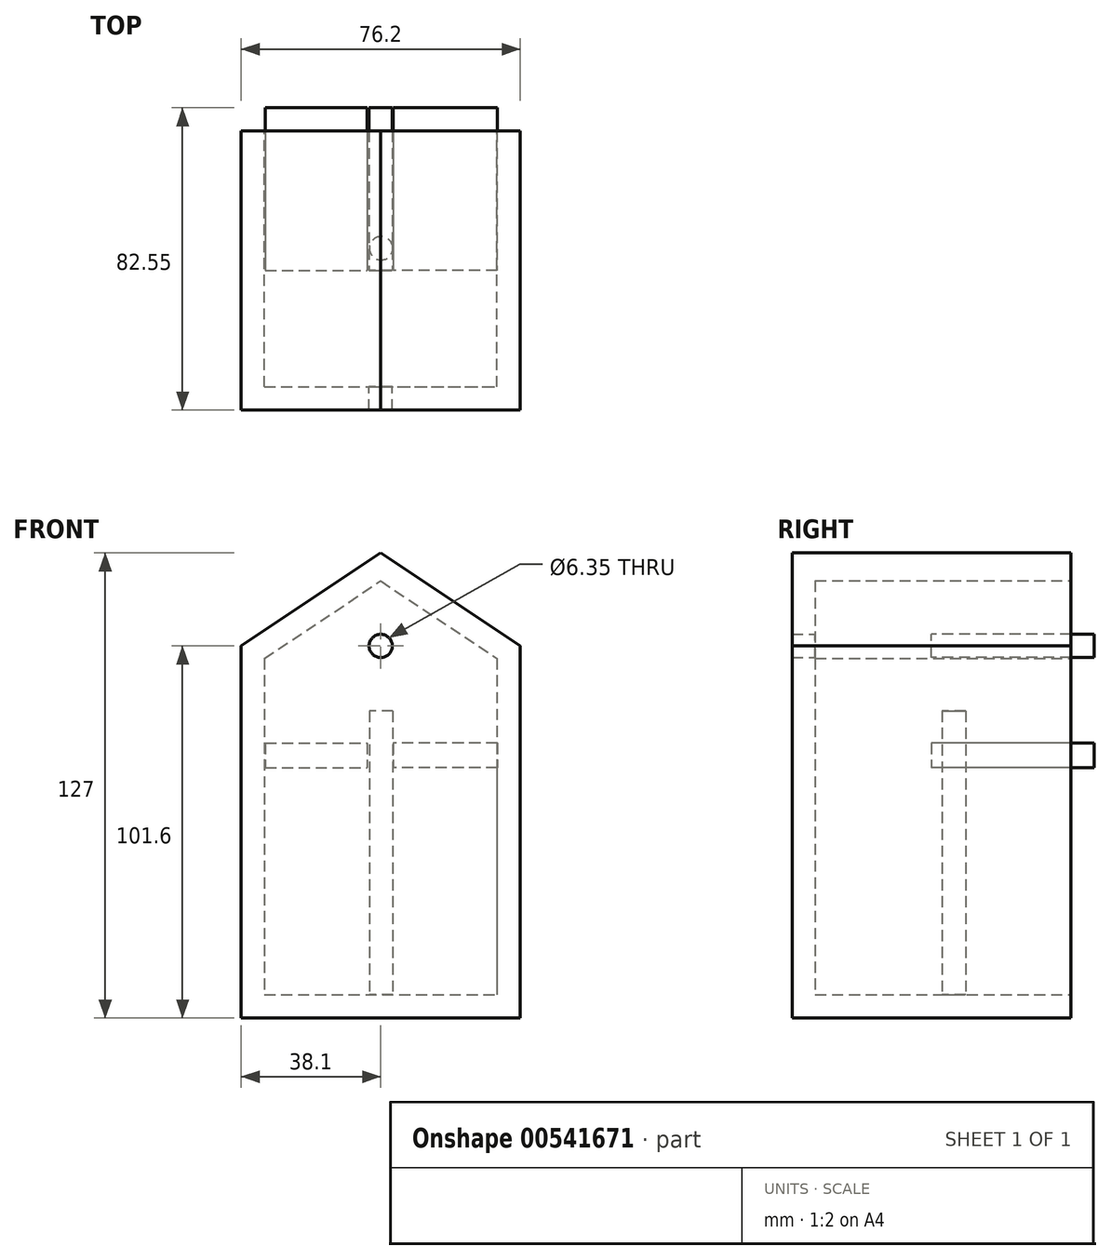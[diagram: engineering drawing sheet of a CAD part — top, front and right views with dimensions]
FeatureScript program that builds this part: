
annotation { "Feature Type Name" : "Feature", "Feature Type Description" : "" }
export const myFeature = defineFeature(function(context is Context, id is Id, definition is map)
    precondition{}
    {
        {
            var Q0;
            Q0=qCreatedBy(makeId("Front.planeOp"),FACE);
            var sketch = newSketch(context, id + "F0", { "sketchPlane" : qUnion([Q0])});
            skLineSegment(sketch, "E0.bottom", {"start": v(-38.1, 50.8) * mm, "end": v(38.1, 50.8) * mm, "construction": true});
            skLineSegment(sketch, "E0.top", {"start": v(-38.1, -50.8) * mm, "end": v(38.1, -50.8) * mm});
            skLineSegment(sketch, "E0.left", {"start": v(-38.1, 50.8) * mm, "end": v(-38.1, -50.8) * mm});
            skLineSegment(sketch, "E0.right", {"start": v(38.1, 50.8) * mm, "end": v(38.1, -50.8) * mm});
            skLineSegment(sketch, "E1", {"start": v(0, 50.8) * mm, "end": v(0, -50.8) * mm, "construction": true});
            skLineSegment(sketch, "E2", {"start": v(-38.1, 50.8) * mm, "end": v(0, 76.2) * mm});
            skLineSegment(sketch, "E3", {"start": v(0, 76.2) * mm, "end": v(38.1, 50.8) * mm});
            skSolve(sketch);
        }
        {
            var Q0;
            Q0=qSketchRegion(id+"F0",true);
            extrude(context, id + "F1", {"entities" : qUnion([Q0]), "endBound" : BoundingType.SYMMETRIC, "depth" : 76.2 * mm});
        }
        {
            var Q0;
            Q0=makeQuery(id+"F1.opExtrude","CAP_FACE",FACE,{"disambiguationData":[OSD([sQuery(id+"F0.wireOp",EDGE,"E0.top"),sQuery(id+"F0.wireOp",EDGE,"E0.left"),sQuery(id+"F0.wireOp",EDGE,"E0.right"),sQuery(id+"F0.wireOp",EDGE,"E2"),sQuery(id+"F0.wireOp",EDGE,"E3")])],"isStart":true});
            shell(context, id + "F2", {"entities" : qUnion([Q0]), "thickness" : 6.35 * mm});
        }
        {
            var Q0;
            Q0=makeQuery(id+"F0.imprint","IMPRINT",FACE,{"disambiguationData":[TD([[makeQuery(id+"F0.imprint","IMPRINT",EDGE,{"derivedFrom":sQuery(id+"F0.wireOp",EDGE,"E0.top")}),1.0]])]});
            var sketch = newSketch(context, id + "F3", { "sketchPlane" : qUnion([Q0])});
            skLineSegment(sketch, "E4.bottom", {"start": v(31.85, 24.31) * mm, "end": v(3.36, 24.31) * mm});
            skLineSegment(sketch, "E4.top", {"start": v(31.85, 17.54) * mm, "end": v(3.36, 17.54) * mm});
            skLineSegment(sketch, "E4.left", {"start": v(31.85, 24.31) * mm, "end": v(31.85, 17.54) * mm});
            skLineSegment(sketch, "E4.right", {"start": v(3.36, 24.31) * mm, "end": v(3.36, 17.54) * mm});
            skLineSegment(sketch, "E5.bottom", {"start": v(-31.54, 24.31) * mm, "end": v(-3.74, 24.31) * mm});
            skLineSegment(sketch, "E5.top", {"start": v(-31.54, 17.54) * mm, "end": v(-3.74, 17.54) * mm});
            skLineSegment(sketch, "E5.left", {"start": v(-31.54, 24.31) * mm, "end": v(-31.54, 17.54) * mm});
            skLineSegment(sketch, "E5.right", {"start": v(-3.74, 24.31) * mm, "end": v(-3.74, 17.54) * mm});
            skSolve(sketch);
        }
        {
            var Q0;
            Q0=sQuery(id+"F3.wireOp",EDGE,"E4.bottom");
            var Q1;
            Q1=sQuery(id+"F3.wireOp",EDGE,"E4.right");
            var Q2;
            Q2=sQuery(id+"F3.wireOp",EDGE,"E4.top");
            var Q3;
            Q3=sQuery(id+"F3.wireOp",EDGE,"E4.left");
            var Q4;
            Q4=sQuery(id+"F3.wireOp",EDGE,"E5.right");
            var Q5;
            Q5=sQuery(id+"F3.wireOp",EDGE,"E5.bottom");
            var Q6;
            Q6=sQuery(id+"F3.wireOp",EDGE,"E5.top");
            var Q7;
            Q7=sQuery(id+"F3.wireOp",EDGE,"E5.left");
            extrude(context, id + "F4", {"bodyType" : ToolBodyType.SURFACE, "surfaceEntities" : qUnion([Q0, Q1, Q2, Q3, Q4, Q5, Q6, Q7]), "endBound" : BoundingType.SYMMETRIC, "oppositeDirection" : true, "depth" : 76.2 * mm});
        }
        {
            var Q0;
            Q0=makeQuery(id+"F2.opShell","OFFSET_FACE",FACE,{"disambiguationData":[OSD([sQuery(id+"F0.wireOp",EDGE,"E0.top")])]});
            var sketch = newSketch(context, id + "F5", { "sketchPlane" : qUnion([Q0])});
            skCircle(sketch, "E6", {"center": v(0.09, 6.08) * mm, "radius": 3.2 * mm});
            skSolve(sketch);
        }
        {
            var Q0;
            Q0=qSketchRegion(id+"F5",true);
            extrude(context, id + "F6", {"entities" : qUnion([Q0]), "operationType" : NewBodyOperationType.ADD, "depth" : 77.51 * mm});
        }
        {
            var Q0;
            Q0=makeQuery(id+"F3.imprint","IMPRINT",FACE,{"disambiguationData":[TD([[makeQuery(id+"F3.imprint","IMPRINT",EDGE,{"derivedFrom":sQuery(id+"F3.wireOp",EDGE,"E4.bottom")}),-1.0]])]});
            var sketch = newSketch(context, id + "F7", { "sketchPlane" : qUnion([Q0])});
            skCircle(sketch, "E7", {"center": v(0, 50.8) * mm, "radius": 3.18 * mm});
            skSolve(sketch);
        }
        {
            var Q0;
            Q0=qSketchRegion(id+"F7",true);
            extrude(context, id + "F8", {"entities" : qUnion([Q0]), "operationType" : NewBodyOperationType.REMOVE, "endBound" : BoundingType.THROUGH_ALL, "depth" : 50.8 * mm});
        }
        {
            var Q0;
            Q0=qSketchRegion(id+"F7",true);
            extrude(context, id + "F10", {"entities" : qUnion([Q0]), "oppositeDirection" : true, "depth" : 44.45 * mm});
        }
        {
            var Q0;
            Q0=qSketchRegion(id+"F3",true);
            extrude(context, id + "F12", {"entities" : qUnion([Q0]), "operationType" : NewBodyOperationType.ADD, "oppositeDirection" : true, "depth" : 44.45 * mm});
        }
        {
            var Q0;
            Q0=qConstructionFilter(qBodyType(qCreatedBy(id+"F5",EDGE),BodyType.WIRE),ConstructionObject.NO);
            extrude(context, id + "F13", {"bodyType" : ToolBodyType.SURFACE, "surfaceEntities" : qUnion([Q0]), "oppositeDirection" : true, "depth" : 31.75 * mm});
        }
    });
